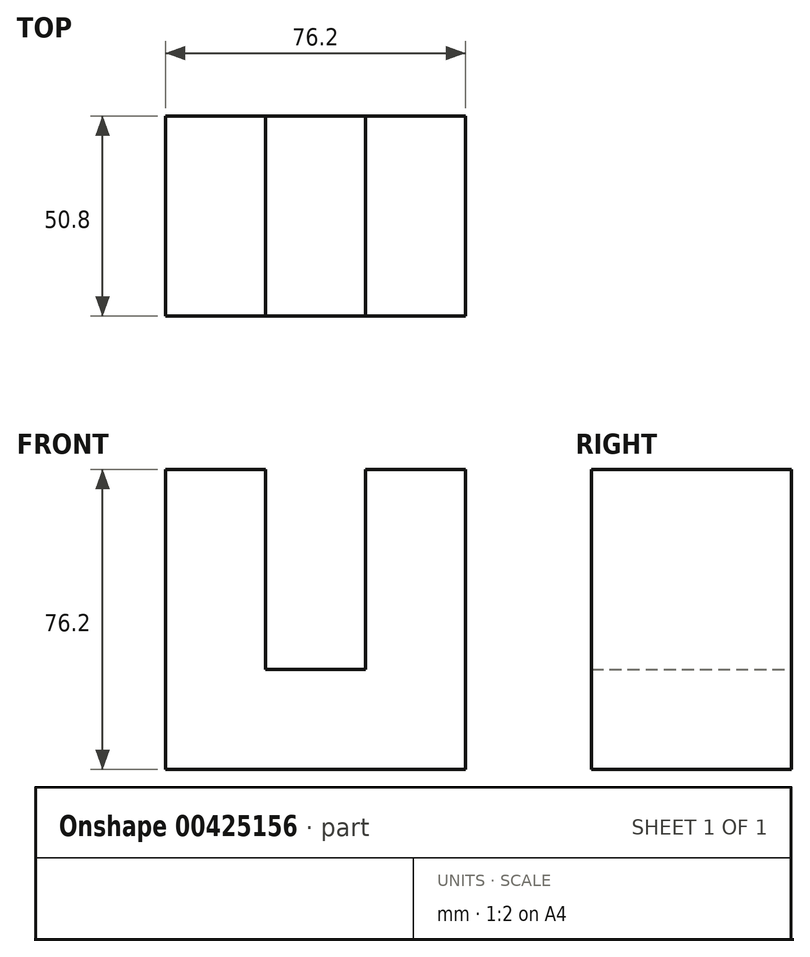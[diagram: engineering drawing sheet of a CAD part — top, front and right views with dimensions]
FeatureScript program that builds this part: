
annotation { "Feature Type Name" : "Feature", "Feature Type Description" : "" }
export const myFeature = defineFeature(function(context is Context, id is Id, definition is map)
    precondition{}
    {
        {
            var Q0;
            Q0=qCreatedBy(makeId("Front.planeOp"),FACE);
            var sketch = newSketch(context, id + "F0", { "sketchPlane" : qUnion([Q0])});
            skLineSegment(sketch, "E0", {"start": v(-50.8, 0) * mm, "end": v(25.4, 0) * mm});
            skLineSegment(sketch, "E1", {"start": v(25.4, 0) * mm, "end": v(25.4, 76.2) * mm});
            skLineSegment(sketch, "E2", {"start": v(25.4, 76.2) * mm, "end": v(0, 76.2) * mm});
            skLineSegment(sketch, "E3", {"start": v(-50.8, 0) * mm, "end": v(-50.8, 76.2) * mm});
            skLineSegment(sketch, "E4", {"start": v(-50.8, 76.2) * mm, "end": v(-25.4, 76.2) * mm});
            skLineSegment(sketch, "E5", {"start": v(-25.4, 76.2) * mm, "end": v(-25.4, 25.4) * mm});
            skLineSegment(sketch, "E6", {"start": v(-25.4, 25.4) * mm, "end": v(0, 25.4) * mm});
            skLineSegment(sketch, "E7", {"start": v(0, 25.4) * mm, "end": v(0, 76.2) * mm});
            skSolve(sketch);
        }
        {
            var Q0;
            Q0 = qSketchRegion(id + "F0", true);
            extrude(context, id + "F1", {"entities" : qUnion([Q0]), "depth" : 50.8 * mm});
        }
    });
